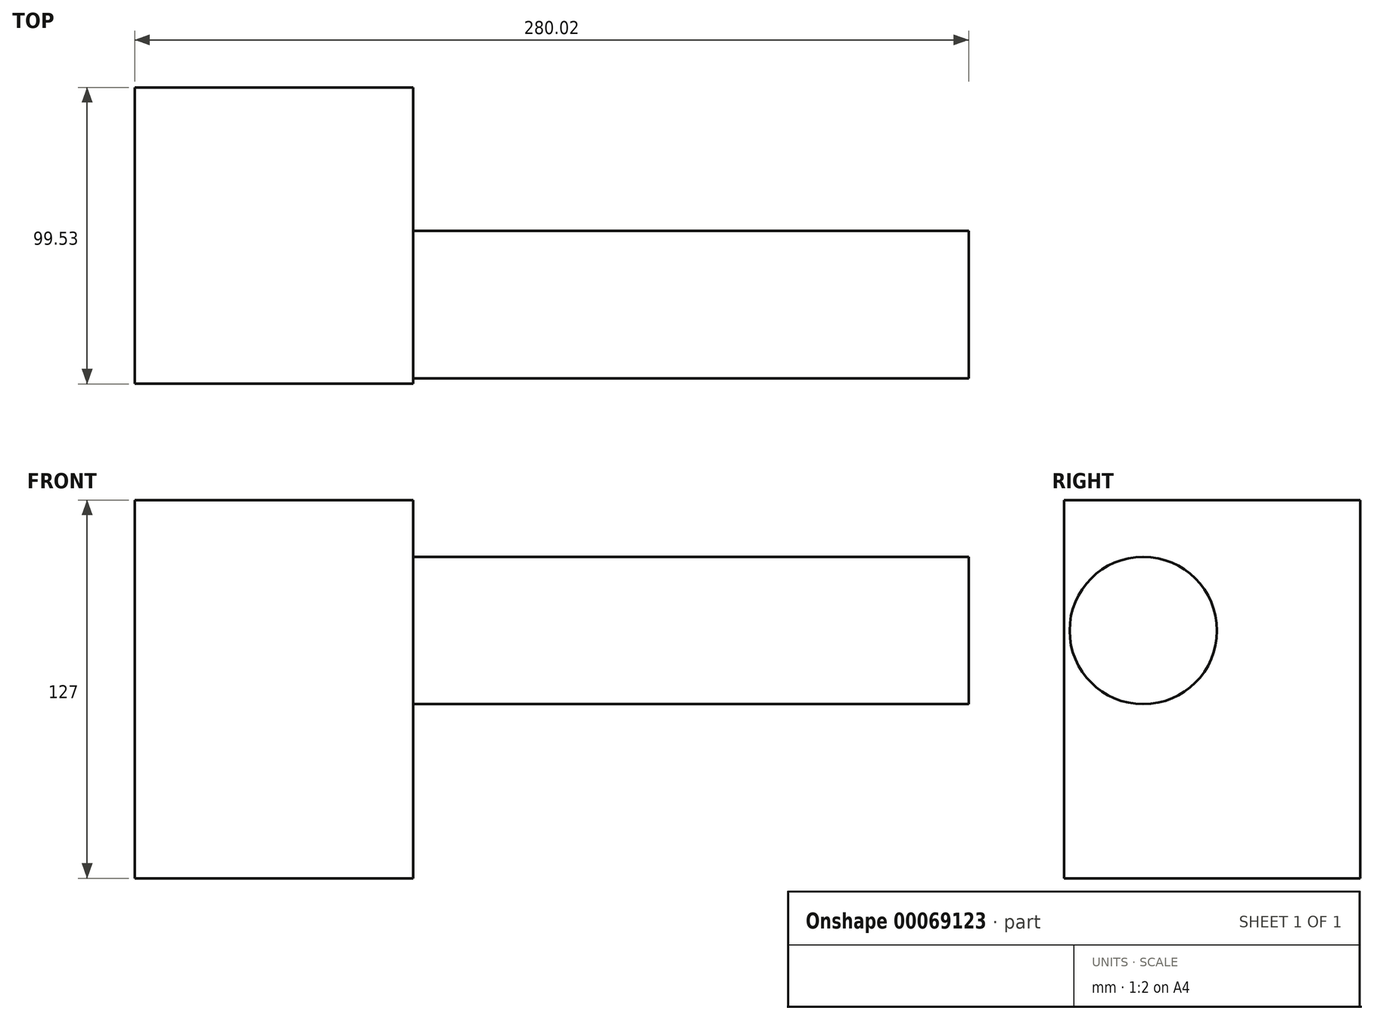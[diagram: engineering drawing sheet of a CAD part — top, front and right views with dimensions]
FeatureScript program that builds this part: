
annotation { "Feature Type Name" : "Feature", "Feature Type Description" : "" }
export const myFeature = defineFeature(function(context is Context, id is Id, definition is map)
    precondition{}
    {
        {
            var Q0;
            Q0=qCreatedBy(makeId("Top.planeOp"),FACE);
            var sketch = newSketch(context, id + "F0", { "sketchPlane" : qUnion([Q0])});
            skLineSegment(sketch, "E0.bottom", {"start": v(-42.95, 48.38) * mm, "end": v(50.57, 48.38) * mm});
            skLineSegment(sketch, "E0.top", {"start": v(-42.95, -51.15) * mm, "end": v(50.57, -51.15) * mm});
            skLineSegment(sketch, "E0.left", {"start": v(-42.95, 48.38) * mm, "end": v(-42.95, -51.15) * mm});
            skLineSegment(sketch, "E0.right", {"start": v(50.57, 48.38) * mm, "end": v(50.57, -51.15) * mm});
            skSolve(sketch);
        }
        {
            var Q0;
            Q0=makeQuery(id+"F0.imprint","IMPRINT",FACE,{"disambiguationData":[TD([[makeQuery(id+"F0.imprint","IMPRINT",EDGE,{"derivedFrom":sQuery(id+"F0.wireOp",EDGE,"E0.bottom")}),-1.0]])]});
            extrude(context, id + "F1", {"entities" : qUnion([Q0]), "depth" : 127 * mm});
        }
        {
            var Q0;
            Q0=makeQuery(id+"F1.opExtrude","SWEPT_FACE",FACE,{"disambiguationData":[OSD([sQuery(id+"F0.wireOp",EDGE,"E0.right")])]});
            var sketch = newSketch(context, id + "F2", { "sketchPlane" : qUnion([Q0])});
            skCircle(sketch, "E1", {"center": v(-24.55, 83.17) * mm, "radius": 24.73 * mm});
            skPoint(sketch, "E1.first.point", {"position": v(-40.33, 102.22) * mm});
            skPoint(sketch, "E1.second.point", {"position": v(0, 86.2) * mm});
            skPoint(sketch, "E1.third.point", {"position": v(-20.32, 58.8) * mm});
            skSolve(sketch);
        }
        {
            var Q0;
            Q0=makeQuery(id+"F2.imprint","IMPRINT",FACE,{"disambiguationData":[TD([[makeQuery(id+"F2.imprint","IMPRINT",EDGE,{"derivedFrom":sQuery(id+"F2.wireOp",EDGE,"E1")}),1.0]])]});
            extrude(context, id + "F3", {"entities" : qUnion([Q0]), "operationType" : NewBodyOperationType.ADD, "endBound" : BoundingType.THROUGH_ALL, "depth" : 25.4 * mm, "hasSecondDirection" : true, "secondDirectionOppositeDirection" : true, "secondDirectionDepth" : 41.98 * mm});
        }
    });
